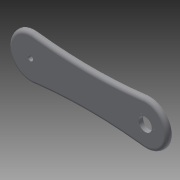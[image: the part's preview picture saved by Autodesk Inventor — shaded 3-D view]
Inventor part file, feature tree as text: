
AUTODESK INVENTOR PART (.ipt)
format: ipt  version: 2015 (Build 190159000, 159)  size: 302,080 bytes
history: native  units: mm
features: sketch x19, extrude x17, fillet x1
ambient origin geometry x8: Origin, YZ Plane, XZ Plane, XY Plane, X Axis, Y Axis, Z Axis, Center Point
bodies: Solid1 (feature_tree)
feature tree (37):
  extrude  "Extrusion1"  Depth=50.0mm
  extrude  "Extrusion2"  Depth=5.0mm
  extrude  "Extrusion3"  Depth=5.0mm TaperAngle=0.0deg
  extrude  "Extrusion4"  Depth=20.0mm
  extrude  "Extrusion5"  Depth=20.0mm
  extrude  "Extrusion6"  Depth=3.0mm
  sketch  "Sketch7"  dims[d22=3.0mm d23=5.0mm d24=0.0mm]
  extrude  "Extrusion7"  Depth=5.0mm TaperAngle=0.0deg
  extrude  "Extrusion8"  Depth=5.0mm
  extrude  "Extrusion9"  Depth=1.0mm
  extrude  "Extrusion10"  Depth=5.0mm
  extrude  "Extrusion11"  Depth=5.0mm TaperAngle=0.0deg
  sketch  "Sketch12"  dims[d44=1.0mm d45=1.0mm]
  sketch  "Sketch13"  dims[d46=1.0mm d47=5.0mm d48=0.0mm]
  extrude  "Extrusion12"  Depth=1.0mm
  extrude  "Extrusion13"  Depth=5.0mm TaperAngle=0.0deg
  extrude  "Extrusion14"  Depth=5.0mm TaperAngle=0.0deg
  extrude  "Extrusion15"  Depth=5.0mm TaperAngle=0.0deg
  extrude  "Extrusion16"  Depth=43.308mm
  sketch  "Sketch18"  dims[d62=33.15mm]
  extrude  "Extrusion18"  Depth=5.0mm
  fillet  "Fillet1"  Radius=5.0mm
  sketch  "Sketch1"  dims[d0=150.0mm d1=50.0mm]
  sketch  "Sketch2"  dims[d2=5.0mm d3=0.0mm d4=6.0mm]
  sketch  "Sketch3"  dims[d5=6.0mm d6=5.0mm d7=0.0mm]
  sketch  "Sketch4"  dims[d11=55.0mm d12=20.0mm]
  sketch  "Sketch5"  dims[d13=40.2mm d14=20.0mm]
  sketch  "Sketch6"  dims[d20=3.0mm d21=3.0mm]
  sketch  "Sketch8"  dims[d32=5.0mm d33=0.0mm d34=1.0mm]
  sketch  "Sketch9"  dims[d35=1.0mm d36=1.0mm]
  sketch  "Sketch10"  dims[d37=5.0mm d38=0.0mm d39=15.0mm]
  sketch  "Sketch11"  dims[d40=15.0mm d41=5.0mm d42=0.0mm]
  sketch  "Sketch14"  dims[d49=5.0mm d50=0.0mm d51=5.0mm d52=0.0mm]
  sketch  "Sketch15"  dims[d53=130.0mm d54=5.0mm d55=0.0mm]
  sketch  "Sketch16"  dims[d56=15.0mm d57=43.308mm]
  sketch  "Sketch17"  dims[d58=40.2mm d59=20.0mm d60=5.0mm d61=0.0mm]
  sketch  "Sketch20"  dims[d63=18.1mm d64=55.0mm d65=40.2mm d66=20.0mm d67=5.0mm d68=0.0mm d69=33.15mm d70=18.1mm d71=55.0mm d72=40.2mm d73=20.0mm d74=5.0mm d75=0.0mm d76=5.0mm d77=0.0mm d84=5.0mm d85=0.0mm d86=5.0mm d87=0.0mm d100=6.0mm d101=5.0mm d102=0.0mm d103=4.0mm]
